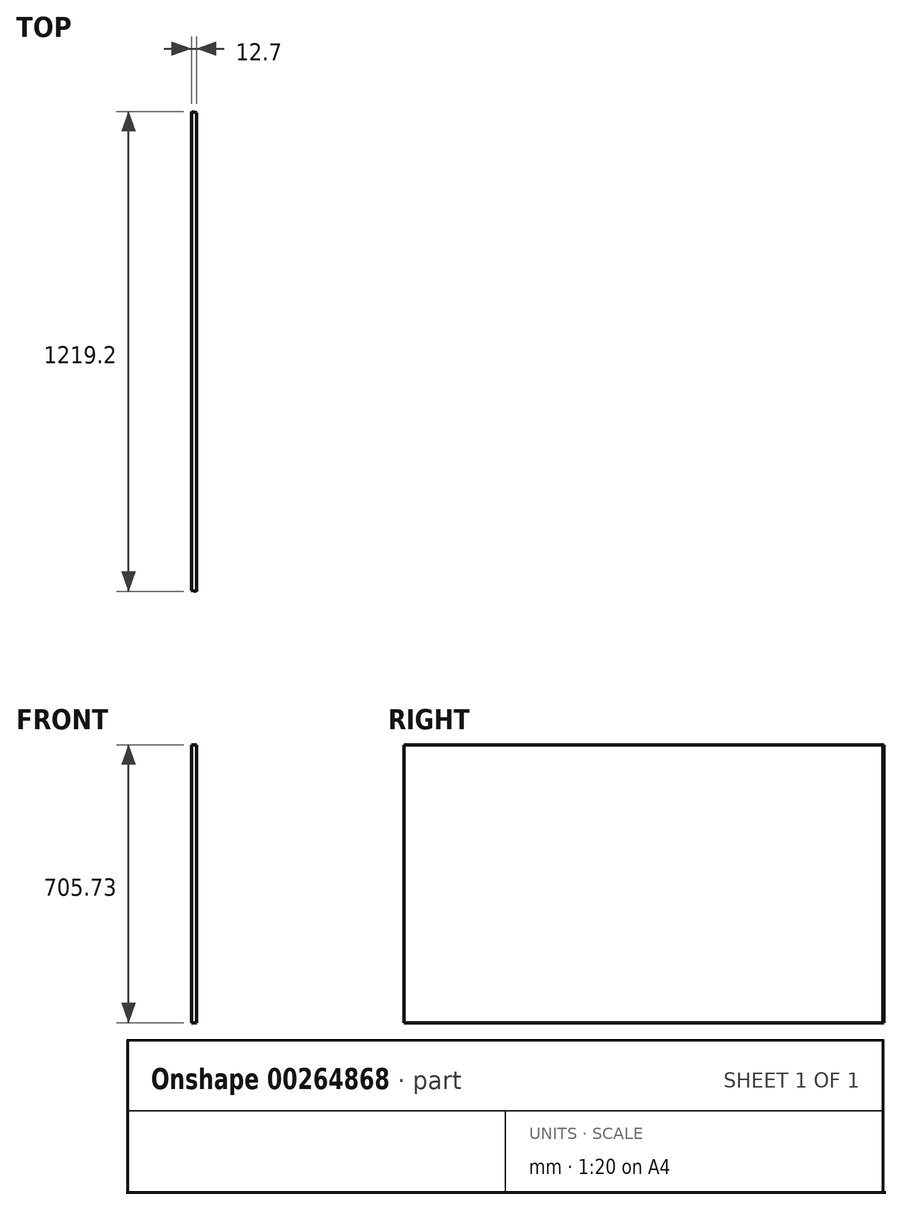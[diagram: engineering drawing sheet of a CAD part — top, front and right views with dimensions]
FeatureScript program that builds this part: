
annotation { "Feature Type Name" : "Feature", "Feature Type Description" : "" }
export const myFeature = defineFeature(function(context is Context, id is Id, definition is map)
    precondition{}
    {
        {
            var Q0;
            Q0=qCreatedBy(makeId("Right.planeOp"),FACE);
            var sketch = newSketch(context, id + "F0", { "sketchPlane" : qUnion([Q0])});
            skLineSegment(sketch, "E0.bottom", {"start": v(-741.28, 359.5) * mm, "end": v(477.92, 359.5) * mm});
            skLineSegment(sketch, "E0.top", {"start": v(-741.28, -346.22) * mm, "end": v(477.92, -346.22) * mm});
            skLineSegment(sketch, "E0.left", {"start": v(-741.28, 359.5) * mm, "end": v(-741.28, -346.22) * mm});
            skLineSegment(sketch, "E0.right", {"start": v(477.92, 359.5) * mm, "end": v(477.92, -346.22) * mm});
            skSolve(sketch);
        }
        {
            var Q0;
            Q0=makeQuery(id+"F0.imprint","IMPRINT",FACE,{"disambiguationData":[TD([[makeQuery(id+"F0.imprint","IMPRINT",EDGE,{"derivedFrom":sQuery(id+"F0.wireOp",EDGE,"E0.bottom")}),-1.0]])]});
            extrude(context, id + "F1", {"entities" : qUnion([Q0]), "depth" : 12.7 * mm});
        }
        {
            var Q0;
            Q0=makeQuery(id+"F1.opExtrude","SWEPT_FACE",FACE,{"disambiguationData":[OSD([sQuery(id+"F0.wireOp",EDGE,"E0.bottom")])]});
            var sketch = newSketch(context, id + "F2", { "sketchPlane" : qUnion([Q0])});
            skLineSegment(sketch, "E1", {"start": v(0, 477.92) * mm, "end": v(40.3, 477.92) * mm});
            skLineSegment(sketch, "E2", {"start": v(40.3, 477.92) * mm, "end": v(40.3, 469.26) * mm});
            skLineSegment(sketch, "E3", {"start": v(40.3, 469.26) * mm, "end": v(0, 477.92) * mm});
            skLineSegment(sketch, "E4", {"start": v(12.7, -741.28) * mm, "end": v(-17.42, -741.28) * mm});
            skLineSegment(sketch, "E5", {"start": v(-17.42, -741.28) * mm, "end": v(-17.42, -734.8) * mm});
            skLineSegment(sketch, "E6", {"start": v(-17.42, -734.8) * mm, "end": v(12.7, -741.28) * mm});
            skSolve(sketch);
        }
        {
            var Q0;
            {var subQ1=sQuery(id+"F2.wireOp",EDGE,"E1");var subQ2=sQuery(id+"F0.wireOp",EDGE,"E0.bottom");var subQ4=makeQuery(id+"F1.opExtrude","CAP_EDGE",EDGE,{"disambiguationData":[OSD([subQ2])],"isStart":false});var subQ5=makeQuery(id+"F2.imprint","INTERSECT",VERTEX,{"derivedFrom":[subQ4,subQ1]});Q0=makeQuery(id+"F2.imprint","IMPRINT",FACE,{"disambiguationData":[TD([[makeQuery(id+"F2.imprint","IMPRINT",EDGE,{"disambiguationData":[TD([[subQ5,1.0]])],"derivedFrom":subQ4}),1.0]])]});}
            var Q1;
            {var subQ0=sQuery(id+"F2.wireOp",EDGE,"E4");var subQ1=sQuery(id+"F0.wireOp",EDGE,"E0.bottom");var subQ2=makeQuery(id+"F1.opExtrude","CAP_EDGE",EDGE,{"disambiguationData":[OSD([subQ1])],"isStart":true});var subQ3=makeQuery(id+"F2.imprint","INTERSECT",VERTEX,{"derivedFrom":[subQ2,subQ0]});Q1=makeQuery(id+"F2.imprint","IMPRINT",FACE,{"disambiguationData":[TD([[makeQuery(id+"F2.imprint","IMPRINT",EDGE,{"disambiguationData":[TD([[subQ3,-1.0]])],"derivedFrom":subQ2}),-1.0]])]});}
            extrude(context, id + "F3", {"entities" : qUnion([Q0, Q1]), "operationType" : NewBodyOperationType.REMOVE, "endBound" : BoundingType.THROUGH_ALL, "oppositeDirection" : true, "depth" : 25.4 * mm, "offsetDistance" : 25.4 * mm});
        }
    });
